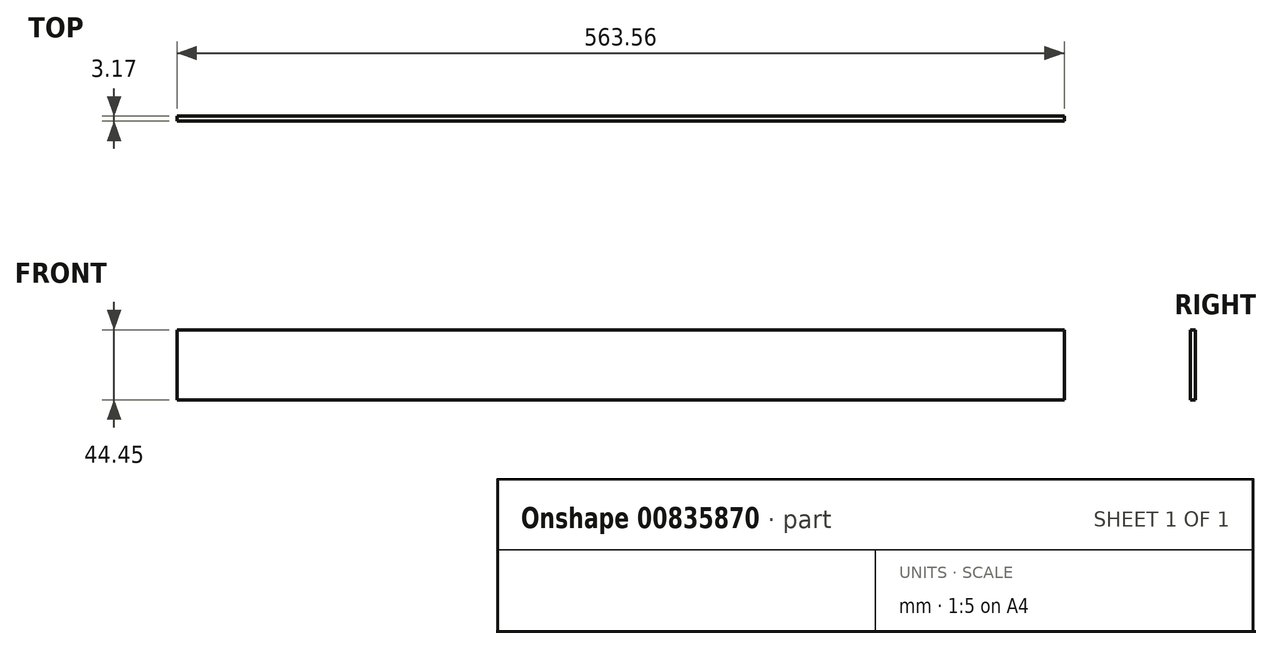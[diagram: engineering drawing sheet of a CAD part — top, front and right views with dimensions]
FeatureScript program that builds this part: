
annotation { "Feature Type Name" : "Feature", "Feature Type Description" : "" }
export const myFeature = defineFeature(function(context is Context, id is Id, definition is map)
    precondition{}
    {
        {
            var Q0;
            Q0=qCreatedBy(makeId("Right.planeOp"),FACE);
            var sketch = newSketch(context, id + "F0", { "sketchPlane" : qUnion([Q0])});
            skLineSegment(sketch, "E0.bottom", {"start": v(0, 0) * mm, "end": v(3.18, 0) * mm});
            skLineSegment(sketch, "E0.top", {"start": v(0, 44.45) * mm, "end": v(3.17, 44.45) * mm});
            skLineSegment(sketch, "E0.left", {"start": v(0, 0) * mm, "end": v(0, 44.45) * mm});
            skLineSegment(sketch, "E0.right", {"start": v(3.18, 0) * mm, "end": v(3.17, 44.45) * mm});
            skSolve(sketch);
        }
        {
            var Q0;
            Q0=qSketchRegion(id+"F0",true);
            extrude(context, id + "F1", {"entities" : qUnion([Q0]), "depth" : 563.56 * mm, "offsetDistance" : 25.4 * mm});
        }
    });
